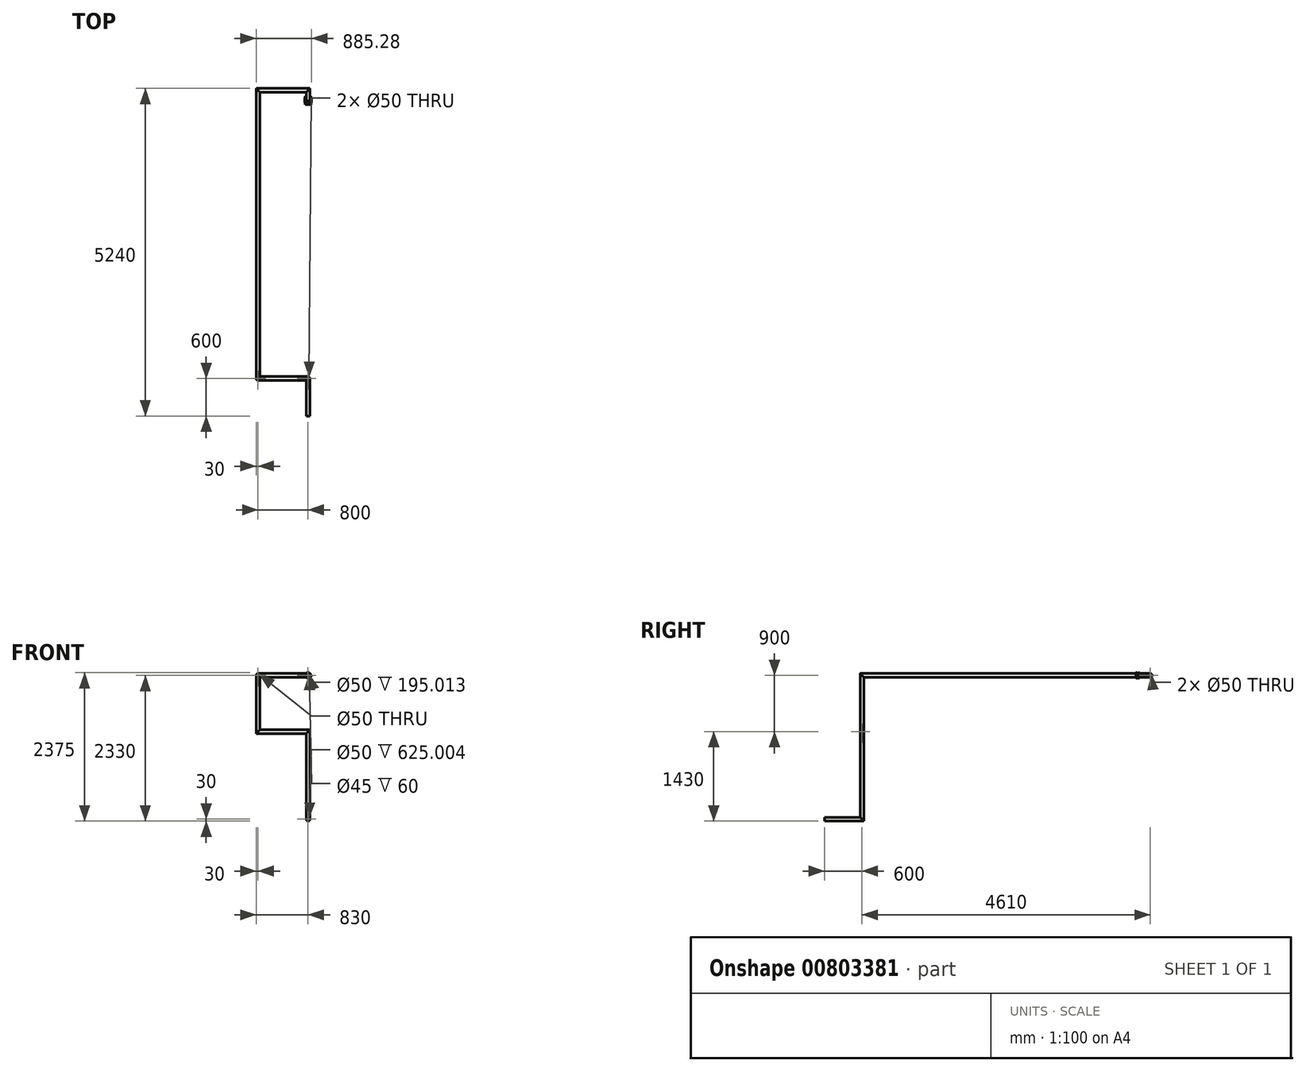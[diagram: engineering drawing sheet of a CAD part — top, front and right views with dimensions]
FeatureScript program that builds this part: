
annotation { "Feature Type Name" : "Feature", "Feature Type Description" : "" }
export const myFeature = defineFeature(function(context is Context, id is Id, definition is map)
    precondition{}
    {
        {
            var Q0;
            Q0=qCreatedBy(makeId("Top.planeOp"),FACE);
            var sketch = newSketch(context, id + "F0", { "sketchPlane" : qUnion([Q0])});
            skLineSegment(sketch, "E0", {"start": v(0, 0) * mm, "end": v(0, 200) * mm});
            skLineSegment(sketch, "E1", {"start": v(0, 200) * mm, "end": v(-800, 200) * mm});
            skLineSegment(sketch, "E2", {"start": v(-800, 200) * mm, "end": v(-800, -4410) * mm});
            skSolve(sketch);
        }
        {
            var Q0;
            Q0=qCreatedBy(makeId("Front.planeOp"),FACE);
            cPlane(context, id + "F1", {"entities" : qUnion([Q0]), "cplaneType" : CPlaneType.OFFSET, "offset" : 4410 * mm, "width" : 150 * mm, "height" : 150 * mm});
        }
        {
            var Q0;
            Q0=qCreatedBy(id+"F1.planeOp",FACE);
            var sketch = newSketch(context, id + "F2", { "sketchPlane" : qUnion([Q0])});
            skPoint(sketch, "E3.0", {"position": v(-800, 0) * mm});
            skLineSegment(sketch, "E4", {"start": v(-800, 0) * mm, "end": v(-800, -900) * mm});
            skLineSegment(sketch, "E5", {"start": v(-800, -900) * mm, "end": v(0, -900) * mm});
            skLineSegment(sketch, "E6", {"start": v(0, -900) * mm, "end": v(0, -2300) * mm});
            skSolve(sketch);
        }
        {
            var Q0;
            Q0=qCreatedBy(makeId("Top.planeOp"),FACE);
            cPlane(context, id + "F3", {"entities" : qUnion([Q0]), "cplaneType" : CPlaneType.OFFSET, "offset" : 2300 * mm, "oppositeDirection" : true, "width" : 150 * mm, "height" : 150 * mm});
        }
        {
            var Q0;
            Q0=qCreatedBy(id+"F3.planeOp",FACE);
            var sketch = newSketch(context, id + "F4", { "sketchPlane" : qUnion([Q0])});
            skPoint(sketch, "E7.0", {"position": v(0, -4410) * mm});
            skLineSegment(sketch, "E8", {"start": v(0, -4410) * mm, "end": v(0, -5010) * mm});
            skSolve(sketch);
        }
        {
            var Q0;
            Q0=qCreatedBy(makeId("Front.planeOp"),FACE);
            var sketch = newSketch(context, id + "F5", { "sketchPlane" : qUnion([Q0])});
            skCircle(sketch, "E9", {"center": v(0, 0) * mm, "radius": 25 * mm});
            skCircle(sketch, "E10", {"center": v(0, 0) * mm, "radius": 30 * mm});
            skSolve(sketch);
        }
        {
            var Q0;
            Q0=makeQuery(id+"F5.imprint","IMPRINT",FACE,{"disambiguationData":[TD([[makeQuery(id+"F5.imprint","IMPRINT",EDGE,{"derivedFrom":sQuery(id+"F5.wireOp",EDGE,"E9")}),-1.0]])]});
            var Q1;
            Q1=sQuery(id+"F0.wireOp",EDGE,"E0");
            var Q2;
            Q2=sQuery(id+"F0.wireOp",EDGE,"E1");
            var Q3;
            Q3=sQuery(id+"F0.wireOp",EDGE,"E2");
            var Q4;
            Q4=sQuery(id+"F2.wireOp",EDGE,"E4");
            var Q5;
            Q5=sQuery(id+"F2.wireOp",EDGE,"E5");
            var Q6;
            Q6=sQuery(id+"F2.wireOp",EDGE,"E6");
            var Q7;
            Q7=sQuery(id+"F4.wireOp",EDGE,"E8");
            sweep(context, id + "F6", {"profiles" : qUnion([Q0]), "path" : qUnion([Q1, Q2, Q3, Q4, Q5, Q6, Q7])});
        }
        {
            var Q0;
            Q0=qCreatedBy(makeId("Top.planeOp"),FACE);
            var sketch = newSketch(context, id + "F7", { "sketchPlane" : qUnion([Q0])});
            skLineSegment(sketch, "E11.bottom", {"start": v(22.5, -30) * mm, "end": v(45, -30) * mm});
            skLineSegment(sketch, "E11.top", {"start": v(22.5, 30) * mm, "end": v(45, 30) * mm});
            skLineSegment(sketch, "E11.right", {"start": v(45, -30) * mm, "end": v(45, -22) * mm});
            skLineSegment(sketch, "E12.bottom", {"start": v(43, 20) * mm, "end": v(42, 20) * mm});
            skLineSegment(sketch, "E12.top", {"start": v(43, -20) * mm, "end": v(42, -20) * mm});
            skLineSegment(sketch, "E12.right", {"start": v(40, 18) * mm, "end": v(40, -18) * mm});
            skLineSegment(sketch, "E13", {"start": v(22.5, -30) * mm, "end": v(22.5, 30) * mm});
            skLineSegment(sketch, "E14.trimOffspring", {"start": v(45, 22) * mm, "end": v(45, 30) * mm});
            skPoint(sketch, "E15.orphan", {"position": v(0, 30) * mm});
            skPoint(sketch, "E16.orphan", {"position": v(0, -30) * mm});
            skPoint(sketch, "E17.visualSharp", {"position": v(45, 20) * mm});
            skArc(sketch, "E17.filletArc", {"start": v(43, 20) * mm, "mid": v(44.41, 20.59) * mm, "end": v(45, 22) * mm});
            skPoint(sketch, "E18.visualSharp", {"position": v(45, -20) * mm});
            skArc(sketch, "E18.filletArc", {"start": v(45, -22) * mm, "mid": v(44.41, -20.59) * mm, "end": v(43, -20) * mm});
            skPoint(sketch, "E19.visualSharp", {"position": v(40, 20) * mm});
            skArc(sketch, "E19.filletArc", {"start": v(42, 20) * mm, "mid": v(40.59, 19.41) * mm, "end": v(40, 18) * mm});
            skPoint(sketch, "E20.visualSharp", {"position": v(40, -20) * mm});
            skArc(sketch, "E20.filletArc", {"start": v(40, -18) * mm, "mid": v(40.59, -19.41) * mm, "end": v(42, -20) * mm});
            skSolve(sketch);
        }
        {
            var Q0;
            Q0=makeQuery(id+"F7.imprint","IMPRINT",FACE,{"disambiguationData":[TD([[makeQuery(id+"F7.imprint","IMPRINT",EDGE,{"derivedFrom":sQuery(id+"F7.wireOp",EDGE,"E11.bottom")}),1.0]])]});
            var Q1;
            Q1=makeQuery(id+"F6.opSweep","SWEPT_FACE",FACE,{"disambiguationData":[OSD([sQuery(id+"F0.wireOp",EDGE,"E0"),sQuery(id+"F5.wireOp",EDGE,"E10")])]});
            revolve(context, id + "F8", {"operationType" : NewBodyOperationType.ADD, "surfaceOperationType" : NewSurfaceOperationType.NEW, "entities" : qUnion([Q0]), "axis" : qUnion([Q1]), "revolveType" : RevolveType.FULL});
        }
        {
            var Q0;
            Q0=qCreatedBy(makeId("Top.planeOp"),FACE);
            var sketch = newSketch(context, id + "F9", { "sketchPlane" : qUnion([Q0])});
            skArc(sketch, "E21", {"start": v(40, -17.54) * mm, "mid": v(47.38, -10.1) * mm, "end": v(50.12, 0) * mm});
            skFitSpline(sketch, "E22", {"points": [v(50.12, 0) * mm, v(54.88, 43.47) * mm, v(44.03, 103.37) * mm, v(51.87, 43.03) * mm, v(49.28, 5.92) * mm], "startDerivative": vector(40.4, 148.5) * mm, "endDerivative": vector(-27.02, -132.88) * mm});
            skArc(sketch, "E23.trimOffspring", {"start": v(49.28, 5.92) * mm, "mid": v(45.77, 12.74) * mm, "end": v(40, 17.79) * mm});
            skLineSegment(sketch, "E24.MirrorCS", {"start": v(-40, 17.79) * mm, "end": v(-40, -17.59) * mm});
            skArc(sketch, "E25.MirrorCS", {"start": v(-49.28, 5.92) * mm, "mid": v(-45.77, 12.74) * mm, "end": v(-40, 17.79) * mm});
            skArc(sketch, "E26.MirrorCS", {"start": v(-40, -17.54) * mm, "mid": v(-47.38, -10.1) * mm, "end": v(-50.12, 0) * mm});
            skFitSpline(sketch, "E27.MirrorCS", {"points": [v(-50.12, 0) * mm, v(-54.88, 43.47) * mm, v(-44.03, 103.37) * mm, v(-51.87, 43.03) * mm, v(-49.28, 5.92) * mm], "startDerivative": vector(-40.4, 148.5) * mm, "endDerivative": vector(27.02, -132.88) * mm});
            skLineSegment(sketch, "E28.bottom", {"start": v(40, 17.79) * mm, "end": v(38.85, 17.79) * mm});
            skLineSegment(sketch, "E28.top", {"start": v(40, -17.52) * mm, "end": v(38.85, -17.52) * mm});
            skLineSegment(sketch, "E28.right", {"start": v(38.85, 17.79) * mm, "end": v(38.85, -17.52) * mm});
            skLineSegment(sketch, "E29.trimOffspring", {"start": v(40, -17.52) * mm, "end": v(40, -17.54) * mm});
            skLineSegment(sketch, "E30.bottom", {"start": v(-40, 17.79) * mm, "end": v(-37.2, 17.79) * mm});
            skLineSegment(sketch, "E30.top", {"start": v(-40, -17.59) * mm, "end": v(-37.2, -17.59) * mm});
            skLineSegment(sketch, "E30.left", {"start": v(-40, -17.54) * mm, "end": v(-40, -17.59) * mm});
            skLineSegment(sketch, "E30.right", {"start": v(-37.2, 17.79) * mm, "end": v(-37.2, -17.59) * mm});
            skPoint(sketch, "E31.orphan", {"position": v(-40, 20) * mm});
            skPoint(sketch, "E32.orphan", {"position": v(-40, -20) * mm});
            skPoint(sketch, "E33.start.orphan", {"position": v(40, 20) * mm});
            skPoint(sketch, "E34.orphan", {"position": v(40, -20) * mm});
            skSolve(sketch);
        }
        {
            var Q0;
            Q0=qCreatedBy(makeId("Right.planeOp"),FACE);
            var sketch = newSketch(context, id + "F10", { "sketchPlane" : qUnion([Q0])});
            skLineSegment(sketch, "E35.bottom", {"start": v(-18.81, 5) * mm, "end": v(18.81, 5) * mm});
            skLineSegment(sketch, "E35.top", {"start": v(-18.81, -5) * mm, "end": v(18.81, -5) * mm});
            skLineSegment(sketch, "E35.left", {"start": v(-18.81, 5) * mm, "end": v(-18.81, -5) * mm});
            skLineSegment(sketch, "E35.right", {"start": v(18.81, 5) * mm, "end": v(18.81, -5) * mm});
            skPoint(sketch, "E35.middle", {"position": v(0, 0) * mm});
            skSolve(sketch);
        }
        {
            var Q0;
            Q0 = qSketchRegion(id + "F10", true);
            extrude(context, id + "F11", {"entities" : qUnion([Q0]), "operationType" : NewBodyOperationType.ADD, "endBound" : BoundingType.SYMMETRIC, "depth" : 85 * mm, "offsetDistance" : 25 * mm});
        }
        {
            var Q0;
            Q0 = qSketchRegion(id + "F9", true);
            extrude(context, id + "F12", {"entities" : qUnion([Q0]), "operationType" : NewBodyOperationType.ADD, "endBound" : BoundingType.SYMMETRIC, "depth" : 10 * mm, "offsetDistance" : 25 * mm});
        }
        {
            var Q0;
            Q0=makeQuery(id+"F11.boolean.opBoolean","SPLIT",FACE,{"disambiguationData":[TD([makeQuery(id+"F8.opRevolve","SWEPT_FACE",FACE,{"disambiguationData":[OSD([sQuery(id+"F7.wireOp",EDGE,"E13")])]})])],"derivedFrom":makeQuery(id+"F11.opExtrude","SWEPT_FACE",FACE,{"disambiguationData":[OSD([sQuery(id+"F10.wireOp",EDGE,"E35.left")])]})});
            extrude(context, id + "F13", {"entities" : qUnion([Q0]), "operationType" : NewBodyOperationType.REMOVE, "oppositeDirection" : true, "depth" : 40 * mm, "offsetDistance" : 25 * mm});
        }
    });
